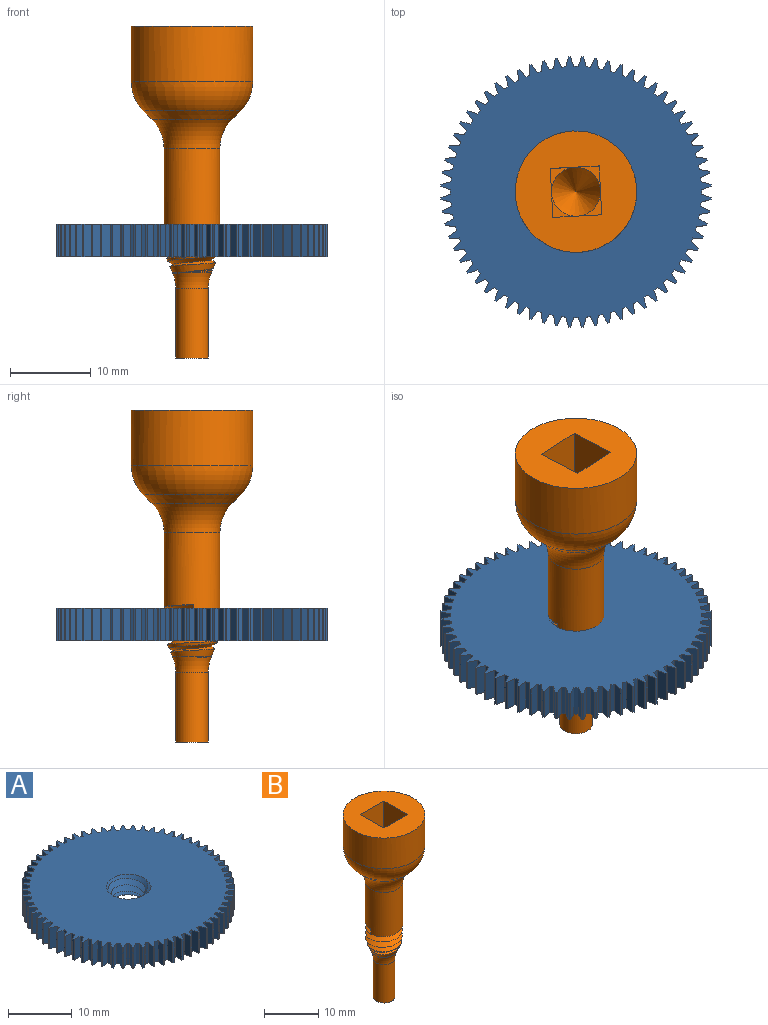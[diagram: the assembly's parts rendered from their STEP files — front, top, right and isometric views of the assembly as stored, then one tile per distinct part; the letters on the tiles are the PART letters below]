
ASSEMBLY  parts=2 mates=1
PART A: 262 faces, bbox 33.4x33.4x5.5 mm
  f0: plane 4x1.22mm, normal (-0.25,0.97,0), area 5.1mm2, adj f1,f255,f256,f257
  f1: cylinder r=15.5mm len=4mm, axis (0,0,-1), area 2.1mm2, adj f0,f2,f255,f257
  f2: plane 4x1.14mm, normal (-0.43,-0.9,0), area 5.1mm2, adj f1,f3,f255,f257
  f3: plane 4x0.24mm, normal (-0.99,0.15,0), area 1mm2, adj f2,f4,f255,f257
  f4: plane 4x1.25mm, normal (-0.15,0.99,0), area 5.1mm2, adj f3,f5,f255,f257
  f5: cylinder r=15.5mm len=4mm, axis (0,0,-1), area 2.1mm2, adj f4,f6,f255,f257
  f6: plane 4x1.08mm, normal (-0.52,-0.85,0), area 5.1mm2, adj f5,f7,f255,f257
  f7: plane 4x0.23mm, normal (-0.97,0.24,0), area 1mm2, adj f6,f8,f255,f257
  f8: plane 4x1.26mm, normal (-0.05,1,0), area 5.1mm2, adj f7,f9,f255,f257
  f9: cylinder r=15.5mm len=4mm, axis (0,0,-1), area 2.1mm2, adj f8,f10,f255,f257
  f10: plane 4x1.01mm, normal (-0.6,-0.8,0), area 5.1mm2, adj f9,f11,f255,f257
  f11: plane 4x0.23mm, normal (-0.94,0.34,0), area 1mm2, adj f10,f12,f255,f257
  f12: plane 4x1.26mm, normal (0.04,1,0), area 5.1mm2, adj f11,f13,f255,f257
  f13: cylinder r=15.5mm len=4mm, axis (0,0,-1), area 2.1mm2, adj f12,f14,f255,f257
  f14: plane 4x0.93mm, normal (-0.68,-0.74,0), area 5.1mm2, adj f13,f15,f255,f257
  f15: plane 4x0.22mm, normal (-0.9,0.43,0), area 1mm2, adj f14,f16,f255,f257
  f16: plane 4x1.25mm, normal (0.14,0.99,0), area 5.1mm2, adj f15,f17,f255,f257
  f17: cylinder r=15.5mm len=4mm, axis (0,0,-1), area 2.1mm2, adj f16,f18,f255,f257
  f18: plane 4x0.94mm, normal (-0.74,-0.67,0), area 5.1mm2, adj f17,f19,f255,f257
  f19: plane 4x0.21mm, normal (-0.86,0.51,0), area 1mm2, adj f18,f20,f255,f257
  f20: plane 4x1.23mm, normal (0.24,0.97,0), area 5.1mm2, adj f19,f21,f255,f257
  f21: cylinder r=15.5mm len=4mm, axis (0,0,-1), area 2.1mm2, adj f20,f22,f255,f257
  f22: plane 4x1.02mm, normal (-0.81,-0.59,0), area 5.1mm2, adj f21,f23,f255,f257
  f23: plane 4x0.19mm, normal (-0.8,0.6,0), area 1mm2, adj f22,f24,f255,f257
  f24: plane 4x1.19mm, normal (0.33,0.94,0), area 5.1mm2, adj f23,f25,f255,f257
  f25: cylinder r=15.5mm len=4mm, axis (0,0,-1), area 2.1mm2, adj f24,f26,f255,f257
  f26: plane 4x1.09mm, normal (-0.86,-0.51,0), area 5.1mm2, adj f25,f27,f255,f257
  f27: plane 4x0.18mm, normal (-0.74,0.67,0), area 1mm2, adj f26,f28,f255,f257
  f28: plane 4x1.15mm, normal (0.42,0.91,0), area 5.1mm2, adj f27,f29,f255,f257
  f29: cylinder r=15.5mm len=4mm, axis (0,0,-1), area 2.1mm2, adj f28,f30,f255,f257
  f30: plane 4x1.15mm, normal (-0.91,-0.42,0), area 5.1mm2, adj f29,f31,f255,f257
  f31: plane 4x0.18mm, normal (-0.67,0.74,0), area 1mm2, adj f30,f32,f255,f257
  f32: plane 4x1.09mm, normal (0.51,0.86,0), area 5.1mm2, adj f31,f33,f255,f257
  f33: cylinder r=15.5mm len=4mm, axis (0,0,-1), area 2.1mm2, adj f32,f34,f255,f257
  f34: plane 4x1.19mm, normal (-0.94,-0.33,0), area 5.1mm2, adj f33,f35,f255,f257
  f35: plane 4x0.19mm, normal (-0.6,0.8,0), area 1mm2, adj f34,f36,f255,f257
  f36: plane 4x1.02mm, normal (0.59,0.81,0), area 5.1mm2, adj f35,f37,f255,f257
  f37: cylinder r=15.5mm len=4mm, axis (0,0,-1), area 2.1mm2, adj f36,f38,f255,f257
  f38: plane 4x1.23mm, normal (-0.97,-0.24,0), area 5.1mm2, adj f37,f39,f255,f257
  f39: plane 4x0.21mm, normal (-0.51,0.86,0), area 1mm2, adj f38,f40,f255,f257
  f40: plane 4x0.94mm, normal (0.67,0.74,0), area 5.1mm2, adj f39,f41,f255,f257
  f41: cylinder r=15.5mm len=4mm, axis (0,0,-1), area 2.1mm2, adj f40,f42,f255,f257
  f42: plane 4x1.25mm, normal (-0.99,-0.14,0), area 5.1mm2, adj f41,f43,f255,f257
  f43: plane 4x0.22mm, normal (-0.43,0.9,0), area 1mm2, adj f42,f44,f255,f257
  f44: plane 4x0.93mm, normal (0.74,0.68,0), area 5.1mm2, adj f43,f45,f255,f257
  f45: cylinder r=15.5mm len=4mm, axis (0,0,-1), area 2.1mm2, adj f44,f46,f255,f257
  f46: plane 4x1.26mm, normal (-1,-0.04,0), area 5.1mm2, adj f45,f47,f255,f257
  f47: plane 4x0.23mm, normal (-0.34,0.94,0), area 1mm2, adj f46,f48,f255,f257
  f48: plane 4x1.01mm, normal (0.8,0.6,0), area 5.1mm2, adj f47,f49,f255,f257
  f49: cylinder r=15.5mm len=4mm, axis (0,0,-1), area 2.1mm2, adj f48,f50,f255,f257
  f50: plane 4x1.26mm, normal (-1,0.05,0), area 5.1mm2, adj f49,f51,f255,f257
  f51: plane 4x0.23mm, normal (-0.24,0.97,0), area 1mm2, adj f50,f52,f255,f257
  f52: plane 4x1.08mm, normal (0.85,0.52,0), area 5.1mm2, adj f51,f53,f255,f257
  f53: cylinder r=15.5mm len=4mm, axis (0,0,-1), area 2.1mm2, adj f52,f54,f255,f257
  f54: plane 4x1.25mm, normal (-0.99,0.15,0), area 5.1mm2, adj f53,f55,f255,f257
  f55: plane 4x0.24mm, normal (-0.15,0.99,0), area 1mm2, adj f54,f56,f255,f257
  f56: plane 4x1.14mm, normal (0.9,0.43,0), area 5.1mm2, adj f55,f57,f255,f257
  f57: cylinder r=15.5mm len=4mm, axis (0,0,-1), area 2.1mm2, adj f56,f58,f255,f257
  f58: plane 4x1.22mm, normal (-0.97,0.25,0), area 5.1mm2, adj f57,f59,f255,f257
  f59: plane 4x0.24mm, normal (-0.05,1,0), area 1mm2, adj f58,f60,f255,f257
  f60: plane 4x1.19mm, normal (0.94,0.34,0), area 5.1mm2, adj f59,f61,f255,f257
  f61: cylinder r=15.5mm len=4mm, axis (0,0,-1), area 2.1mm2, adj f60,f62,f255,f257
  f62: plane 4x1.19mm, normal (-0.94,0.34,0), area 5.1mm2, adj f61,f63,f255,f257
  f63: plane 4x0.24mm, normal (0.05,1,0), area 1mm2, adj f62,f64,f255,f257
  f64: plane 4x1.22mm, normal (0.97,0.25,0), area 5.1mm2, adj f63,f65,f255,f257
  f65: cylinder r=15.5mm len=4mm, axis (0,0,-1), area 2.1mm2, adj f64,f66,f255,f257
  f66: plane 4x1.14mm, normal (-0.9,0.43,0), area 5.1mm2, adj f65,f67,f255,f257
  f67: plane 4x0.24mm, normal (0.15,0.99,0), area 1mm2, adj f66,f68,f255,f257
  f68: plane 4x1.25mm, normal (0.99,0.15,0), area 5.1mm2, adj f67,f69,f255,f257
  f69: cylinder r=15.5mm len=4mm, axis (0,0,-1), area 2.1mm2, adj f68,f70,f255,f257
  f70: plane 4x1.08mm, normal (-0.85,0.52,0), area 5.1mm2, adj f69,f71,f255,f257
  f71: plane 4x0.23mm, normal (0.24,0.97,0), area 1mm2, adj f70,f72,f255,f257
  f72: plane 4x1.26mm, normal (1,0.05,0), area 5.1mm2, adj f71,f73,f255,f257
  f73: cylinder r=15.5mm len=4mm, axis (0,0,-1), area 2.1mm2, adj f72,f74,f255,f257
  f74: plane 4x1.01mm, normal (-0.8,0.6,0), area 5.1mm2, adj f73,f75,f255,f257
  f75: plane 4x0.23mm, normal (0.34,0.94,0), area 1mm2, adj f74,f76,f255,f257
  f76: plane 4x1.26mm, normal (1,-0.04,0), area 5.1mm2, adj f75,f77,f255,f257
  f77: cylinder r=15.5mm len=4mm, axis (0,0,-1), area 2.1mm2, adj f76,f78,f255,f257
  f78: plane 4x0.93mm, normal (-0.74,0.68,0), area 5.1mm2, adj f77,f79,f255,f257
  f79: plane 4x0.22mm, normal (0.43,0.9,0), area 1mm2, adj f78,f80,f255,f257
  f80: plane 4x1.25mm, normal (0.99,-0.14,0), area 5.1mm2, adj f79,f81,f255,f257
  f81: cylinder r=15.5mm len=4mm, axis (0,0,-1), area 2.1mm2, adj f80,f82,f255,f257
  f82: plane 4x0.94mm, normal (-0.67,0.74,0), area 5.1mm2, adj f81,f83,f255,f257
  f83: plane 4x0.21mm, normal (0.51,0.86,0), area 1mm2, adj f82,f84,f255,f257
  f84: plane 4x1.23mm, normal (0.97,-0.24,0), area 5.1mm2, adj f83,f85,f255,f257
  f85: cylinder r=15.5mm len=4mm, axis (0,0,-1), area 2.1mm2, adj f84,f86,f255,f257
  f86: plane 4x1.02mm, normal (-0.59,0.81,0), area 5.1mm2, adj f85,f87,f255,f257
  f87: plane 4x0.19mm, normal (0.6,0.8,0), area 1mm2, adj f86,f88,f255,f257
  f88: plane 4x1.19mm, normal (0.94,-0.33,0), area 5.1mm2, adj f87,f89,f255,f257
  f89: cylinder r=15.5mm len=4mm, axis (0,0,-1), area 2.1mm2, adj f88,f90,f255,f257
  f90: plane 4x1.09mm, normal (-0.51,0.86,0), area 5.1mm2, adj f89,f91,f255,f257
  f91: plane 4x0.18mm, normal (0.67,0.74,0), area 1mm2, adj f90,f92,f255,f257
  f92: plane 4x1.15mm, normal (0.91,-0.42,0), area 5.1mm2, adj f91,f93,f255,f257
  f93: cylinder r=15.5mm len=4mm, axis (0,0,-1), area 2.1mm2, adj f92,f94,f255,f257
  f94: plane 4x1.15mm, normal (-0.42,0.91,0), area 5.1mm2, adj f93,f95,f255,f257
  f95: plane 4x0.18mm, normal (0.74,0.67,0), area 1mm2, adj f94,f96,f255,f257
  f96: plane 4x1.09mm, normal (0.86,-0.51,0), area 5.1mm2, adj f95,f97,f255,f257
  f97: cylinder r=15.5mm len=4mm, axis (0,0,-1), area 2.1mm2, adj f96,f98,f255,f257
  f98: plane 4x1.19mm, normal (-0.33,0.94,0), area 5.1mm2, adj f97,f99,f255,f257
  f99: plane 4x0.19mm, normal (0.8,0.6,0), area 1mm2, adj f98,f100,f255,f257
  f100: plane 4x1.02mm, normal (0.81,-0.59,0), area 5.1mm2, adj f99,f101,f255,f257
  f101: cylinder r=15.5mm len=4mm, axis (0,0,-1), area 2.1mm2, adj f100,f102,f255,f257
  f102: plane 4x1.23mm, normal (-0.24,0.97,0), area 5.1mm2, adj f101,f103,f255,f257
  f103: plane 4x0.21mm, normal (0.86,0.51,0), area 1mm2, adj f102,f104,f255,f257
  f104: plane 4x0.94mm, normal (0.74,-0.67,0), area 5.1mm2, adj f103,f105,f255,f257
  f105: cylinder r=15.5mm len=4mm, axis (0,0,-1), area 2.1mm2, adj f104,f106,f255,f257
  f106: plane 4x1.25mm, normal (-0.14,0.99,0), area 5.1mm2, adj f105,f107,f255,f257
  f107: plane 4x0.22mm, normal (0.9,0.43,0), area 1mm2, adj f106,f108,f255,f257
  f108: plane 4x0.93mm, normal (0.68,-0.74,0), area 5.1mm2, adj f107,f109,f255,f257
  f109: cylinder r=15.5mm len=4mm, axis (0,0,-1), area 2.1mm2, adj f108,f110,f255,f257
  f110: plane 4x1.26mm, normal (-0.04,1,0), area 5.1mm2, adj f109,f111,f255,f257
  f111: plane 4x0.23mm, normal (0.94,0.34,0), area 1mm2, adj f110,f112,f255,f257
  f112: plane 4x1.01mm, normal (0.6,-0.8,0), area 5.1mm2, adj f111,f113,f255,f257
  f113: cylinder r=15.5mm len=4mm, axis (0,0,-1), area 2.1mm2, adj f112,f114,f255,f257
  f114: plane 4x1.26mm, normal (0.05,1,0), area 5.1mm2, adj f113,f115,f255,f257
  f115: plane 4x0.23mm, normal (0.97,0.24,0), area 1mm2, adj f114,f116,f255,f257
  f116: plane 4x1.08mm, normal (0.52,-0.85,0), area 5.1mm2, adj f115,f117,f255,f257
  f117: cylinder r=15.5mm len=4mm, axis (0,0,-1), area 2.1mm2, adj f116,f118,f255,f257
  f118: plane 4x1.25mm, normal (0.15,0.99,0), area 5.1mm2, adj f117,f119,f255,f257
  f119: plane 4x0.24mm, normal (0.99,0.15,0), area 1mm2, adj f118,f120,f255,f257
  f120: plane 4x1.14mm, normal (0.43,-0.9,0), area 5.1mm2, adj f119,f121,f255,f257
  f121: cylinder r=15.5mm len=4mm, axis (0,0,-1), area 2.1mm2, adj f120,f122,f255,f257
  f122: plane 4x1.22mm, normal (0.25,0.97,0), area 5.1mm2, adj f121,f123,f255,f257
  f123: plane 4x0.24mm, normal (1,0.05,0), area 1mm2, adj f122,f124,f255,f257
  f124: plane 4x1.19mm, normal (0.34,-0.94,0), area 5.1mm2, adj f123,f125,f255,f257
  f125: cylinder r=15.5mm len=4mm, axis (0,0,-1), area 2.1mm2, adj f124,f126,f255,f257
  f126: plane 4x1.19mm, normal (0.34,0.94,0), area 5.1mm2, adj f125,f127,f255,f257
  f127: plane 4x0.24mm, normal (1,-0.05,0), area 1mm2, adj f126,f128,f255,f257
  f128: plane 4x1.22mm, normal (0.25,-0.97,0), area 5.1mm2, adj f127,f129,f255,f257
  f129: cylinder r=15.5mm len=4mm, axis (0,0,-1), area 2.1mm2, adj f128,f130,f255,f257
  f130: plane 4x1.14mm, normal (0.43,0.9,0), area 5.1mm2, adj f129,f131,f255,f257
  f131: plane 4x0.24mm, normal (0.99,-0.15,0), area 1mm2, adj f130,f132,f255,f257
  f132: plane 4x1.25mm, normal (0.15,-0.99,0), area 5.1mm2, adj f131,f133,f255,f257
  f133: cylinder r=15.5mm len=4mm, axis (0,0,-1), area 2.1mm2, adj f132,f134,f255,f257
  f134: plane 4x1.08mm, normal (0.52,0.85,0), area 5.1mm2, adj f133,f135,f255,f257
  f135: plane 4x0.23mm, normal (0.97,-0.24,0), area 1mm2, adj f134,f136,f255,f257
  f136: plane 4x1.26mm, normal (0.05,-1,0), area 5.1mm2, adj f135,f137,f255,f257
  f137: cylinder r=15.5mm len=4mm, axis (0,0,-1), area 2.1mm2, adj f136,f138,f255,f257
  f138: plane 4x1.01mm, normal (0.6,0.8,0), area 5.1mm2, adj f137,f139,f255,f257
  f139: plane 4x0.23mm, normal (0.94,-0.34,0), area 1mm2, adj f138,f140,f255,f257
  f140: plane 4x1.26mm, normal (-0.04,-1,0), area 5.1mm2, adj f139,f141,f255,f257
  f141: cylinder r=15.5mm len=4mm, axis (0,0,-1), area 2.1mm2, adj f140,f142,f255,f257
  f142: plane 4x0.93mm, normal (0.68,0.74,0), area 5.1mm2, adj f141,f143,f255,f257
  f143: plane 4x0.22mm, normal (0.9,-0.43,0), area 1mm2, adj f142,f144,f255,f257
  f144: plane 4x1.25mm, normal (-0.14,-0.99,0), area 5.1mm2, adj f143,f145,f255,f257
  f145: cylinder r=15.5mm len=4mm, axis (0,0,-1), area 2.1mm2, adj f144,f146,f255,f257
  f146: plane 4x0.94mm, normal (0.74,0.67,0), area 5.1mm2, adj f145,f147,f255,f257
  f147: plane 4x0.21mm, normal (0.86,-0.51,0), area 1mm2, adj f146,f148,f255,f257
  f148: plane 4x1.23mm, normal (-0.24,-0.97,0), area 5.1mm2, adj f147,f149,f255,f257
  f149: cylinder r=15.5mm len=4mm, axis (0,0,-1), area 2.1mm2, adj f148,f150,f255,f257
  f150: plane 4x1.02mm, normal (0.81,0.59,0), area 5.1mm2, adj f149,f151,f255,f257
  f151: plane 4x0.19mm, normal (0.8,-0.6,0), area 1mm2, adj f150,f152,f255,f257
  f152: plane 4x1.19mm, normal (-0.33,-0.94,0), area 5.1mm2, adj f151,f153,f255,f257
  f153: cylinder r=15.5mm len=4mm, axis (0,0,-1), area 2.1mm2, adj f152,f154,f255,f257
  f154: plane 4x1.09mm, normal (0.86,0.51,0), area 5.1mm2, adj f153,f155,f255,f257
  f155: plane 4x0.18mm, normal (0.74,-0.67,0), area 1mm2, adj f154,f156,f255,f257
  f156: plane 4x1.15mm, normal (-0.42,-0.91,0), area 5.1mm2, adj f155,f157,f255,f257
  f157: cylinder r=15.5mm len=4mm, axis (0,0,-1), area 2.1mm2, adj f156,f158,f255,f257
  f158: plane 4x1.15mm, normal (0.91,0.42,0), area 5.1mm2, adj f157,f159,f255,f257
  f159: plane 4x0.18mm, normal (0.67,-0.74,0), area 1mm2, adj f158,f160,f255,f257
  f160: plane 4x1.09mm, normal (-0.51,-0.86,0), area 5.1mm2, adj f159,f161,f255,f257
  f161: cylinder r=15.5mm len=4mm, axis (0,0,-1), area 2.1mm2, adj f160,f162,f255,f257
  f162: plane 4x1.19mm, normal (0.94,0.33,0), area 5.1mm2, adj f161,f163,f255,f257
  f163: plane 4x0.19mm, normal (0.6,-0.8,0), area 1mm2, adj f162,f164,f255,f257
  f164: plane 4x1.02mm, normal (-0.59,-0.81,0), area 5.1mm2, adj f163,f165,f255,f257
  f165: cylinder r=15.5mm len=4mm, axis (0,0,-1), area 2.1mm2, adj f164,f166,f255,f257
  f166: plane 4x1.23mm, normal (0.97,0.24,0), area 5.1mm2, adj f165,f167,f255,f257
  f167: plane 4x0.21mm, normal (0.51,-0.86,0), area 1mm2, adj f166,f168,f255,f257
  f168: plane 4x0.94mm, normal (-0.67,-0.74,0), area 5.1mm2, adj f167,f169,f255,f257
  f169: cylinder r=15.5mm len=4mm, axis (0,0,-1), area 2.1mm2, adj f168,f170,f255,f257
  f170: plane 4x1.25mm, normal (0.99,0.14,0), area 5.1mm2, adj f169,f171,f255,f257
  f171: plane 4x0.22mm, normal (0.43,-0.9,0), area 1mm2, adj f170,f172,f255,f257
  f172: plane 4x0.93mm, normal (-0.74,-0.68,0), area 5.1mm2, adj f171,f173,f255,f257
  f173: cylinder r=15.5mm len=4mm, axis (0,0,-1), area 2.1mm2, adj f172,f174,f255,f257
  f174: plane 4x1.26mm, normal (1,0.04,0), area 5.1mm2, adj f173,f175,f255,f257
  f175: plane 4x0.23mm, normal (0.34,-0.94,0), area 1mm2, adj f174,f176,f255,f257
  f176: plane 4x1.01mm, normal (-0.8,-0.6,0), area 5.1mm2, adj f175,f177,f255,f257
  f177: cylinder r=15.5mm len=4mm, axis (0,0,-1), area 2.1mm2, adj f176,f178,f255,f257
  f178: plane 4x1.26mm, normal (1,-0.05,0), area 5.1mm2, adj f177,f179,f255,f257
  f179: plane 4x0.23mm, normal (0.24,-0.97,0), area 1mm2, adj f178,f180,f255,f257
  f180: plane 4x1.08mm, normal (-0.85,-0.52,0), area 5.1mm2, adj f179,f181,f255,f257
  f181: cylinder r=15.5mm len=4mm, axis (0,0,-1), area 2.1mm2, adj f180,f182,f255,f257
  f182: plane 4x1.25mm, normal (0.99,-0.15,0), area 5.1mm2, adj f181,f183,f255,f257
  f183: plane 4x0.24mm, normal (0.15,-0.99,0), area 1mm2, adj f182,f184,f255,f257
  f184: plane 4x1.14mm, normal (-0.9,-0.43,0), area 5.1mm2, adj f183,f185,f255,f257
  f185: cylinder r=15.5mm len=4mm, axis (0,0,-1), area 2.1mm2, adj f184,f186,f255,f257
  f186: plane 4x1.22mm, normal (0.97,-0.25,0), area 5.1mm2, adj f185,f187,f255,f257
  f187: plane 4x0.24mm, normal (0.05,-1,0), area 1mm2, adj f186,f188,f255,f257
  f188: plane 4x1.19mm, normal (-0.94,-0.34,0), area 5.1mm2, adj f187,f189,f255,f257
  f189: cylinder r=15.5mm len=4mm, axis (0,0,-1), area 2.1mm2, adj f188,f190,f255,f257
  f190: plane 4x1.19mm, normal (0.94,-0.34,0), area 5.1mm2, adj f189,f191,f255,f257
  f191: plane 4x0.24mm, normal (-0.05,-1,0), area 1mm2, adj f190,f192,f255,f257
  f192: plane 4x1.22mm, normal (-0.97,-0.25,0), area 5.1mm2, adj f191,f193,f255,f257
  f193: cylinder r=15.5mm len=4mm, axis (0,0,-1), area 2.1mm2, adj f192,f194,f255,f257
  f194: plane 4x1.14mm, normal (0.9,-0.43,0), area 5.1mm2, adj f193,f195,f255,f257
  f195: plane 4x0.24mm, normal (-0.15,-0.99,0), area 1mm2, adj f194,f196,f255,f257
  f196: plane 4x1.25mm, normal (-0.99,-0.15,0), area 5.1mm2, adj f195,f197,f255,f257
  f197: cylinder r=15.5mm len=4mm, axis (0,0,-1), area 2.1mm2, adj f196,f198,f255,f257
  f198: plane 4x1.08mm, normal (0.85,-0.52,0), area 5.1mm2, adj f197,f199,f255,f257
  f199: plane 4x0.23mm, normal (-0.24,-0.97,0), area 1mm2, adj f198,f200,f255,f257
  f200: plane 4x1.26mm, normal (-1,-0.05,0), area 5.1mm2, adj f199,f201,f255,f257
  f201: cylinder r=15.5mm len=4mm, axis (0,0,-1), area 2.1mm2, adj f200,f202,f255,f257
  f202: plane 4x1.01mm, normal (0.8,-0.6,0), area 5.1mm2, adj f201,f203,f255,f257
  f203: plane 4x0.23mm, normal (-0.34,-0.94,0), area 1mm2, adj f202,f204,f255,f257
  f204: plane 4x1.26mm, normal (-1,0.04,0), area 5.1mm2, adj f203,f205,f255,f257
  f205: cylinder r=15.5mm len=4mm, axis (0,0,-1), area 2.1mm2, adj f204,f206,f255,f257
  f206: plane 4x0.93mm, normal (0.74,-0.68,0), area 5.1mm2, adj f205,f207,f255,f257
  f207: plane 4x0.22mm, normal (-0.43,-0.9,0), area 1mm2, adj f206,f208,f255,f257
  f208: plane 4x1.25mm, normal (-0.99,0.14,0), area 5.1mm2, adj f207,f209,f255,f257
  f209: cylinder r=15.5mm len=4mm, axis (0,0,-1), area 2.1mm2, adj f208,f210,f255,f257
  f210: plane 4x0.94mm, normal (0.67,-0.74,0), area 5.1mm2, adj f209,f211,f255,f257
  f211: plane 4x0.21mm, normal (-0.51,-0.86,0), area 1mm2, adj f210,f212,f255,f257
  f212: plane 4x1.23mm, normal (-0.97,0.24,0), area 5.1mm2, adj f211,f213,f255,f257
  f213: cylinder r=15.5mm len=4mm, axis (0,0,-1), area 2.1mm2, adj f212,f214,f255,f257
  f214: plane 4x1.02mm, normal (0.59,-0.81,0), area 5.1mm2, adj f213,f215,f255,f257
  f215: plane 4x0.19mm, normal (-0.6,-0.8,0), area 1mm2, adj f214,f216,f255,f257
  f216: plane 4x1.19mm, normal (-0.94,0.33,0), area 5.1mm2, adj f215,f217,f255,f257
  f217: cylinder r=15.5mm len=4mm, axis (0,0,-1), area 2.1mm2, adj f216,f218,f255,f257
  f218: plane 4x1.09mm, normal (0.51,-0.86,0), area 5.1mm2, adj f217,f219,f255,f257
  f219: plane 4x0.18mm, normal (-0.67,-0.74,0), area 1mm2, adj f218,f220,f255,f257
  f220: plane 4x1.15mm, normal (-0.91,0.42,0), area 5.1mm2, adj f219,f221,f255,f257
  f221: cylinder r=15.5mm len=4mm, axis (0,0,-1), area 2.1mm2, adj f220,f222,f255,f257
  f222: plane 4x1.15mm, normal (0.42,-0.91,0), area 5.1mm2, adj f221,f223,f255,f257
  f223: plane 4x0.18mm, normal (-0.74,-0.67,0), area 1mm2, adj f222,f224,f255,f257
  f224: plane 4x1.09mm, normal (-0.86,0.51,0), area 5.1mm2, adj f223,f225,f255,f257
  f225: cylinder r=15.5mm len=4mm, axis (0,0,-1), area 2.1mm2, adj f224,f226,f255,f257
  f226: plane 4x1.19mm, normal (0.33,-0.94,0), area 5.1mm2, adj f225,f227,f255,f257
  f227: plane 4x0.19mm, normal (-0.8,-0.6,0), area 1mm2, adj f226,f228,f255,f257
  f228: plane 4x1.02mm, normal (-0.81,0.59,0), area 5.1mm2, adj f227,f229,f255,f257
  f229: cylinder r=15.5mm len=4mm, axis (0,0,-1), area 2.1mm2, adj f228,f230,f255,f257
  f230: plane 4x1.23mm, normal (0.24,-0.97,0), area 5.1mm2, adj f229,f231,f255,f257
  f231: plane 4x0.21mm, normal (-0.86,-0.51,0), area 1mm2, adj f230,f232,f255,f257
  f232: plane 4x0.94mm, normal (-0.74,0.67,0), area 5.1mm2, adj f231,f233,f255,f257
  f233: cylinder r=15.5mm len=4mm, axis (0,0,-1), area 2.1mm2, adj f232,f234,f255,f257
  f234: plane 4x1.25mm, normal (0.14,-0.99,0), area 5.1mm2, adj f233,f235,f255,f257
  f235: plane 4x0.22mm, normal (-0.9,-0.43,0), area 1mm2, adj f234,f236,f255,f257
  f236: plane 4x0.93mm, normal (-0.68,0.74,0), area 5.1mm2, adj f235,f237,f255,f257
  f237: cylinder r=15.5mm len=4mm, axis (0,0,-1), area 2.1mm2, adj f236,f238,f255,f257
  f238: plane 4x1.26mm, normal (0.04,-1,0), area 5.1mm2, adj f237,f239,f255,f257
  f239: plane 4x0.23mm, normal (-0.94,-0.34,0), area 1mm2, adj f238,f240,f255,f257
  f240: plane 4x1.01mm, normal (-0.6,0.8,0), area 5.1mm2, adj f239,f241,f255,f257
  f241: cylinder r=15.5mm len=4mm, axis (0,0,-1), area 2.1mm2, adj f240,f242,f255,f257
  f242: plane 4x1.26mm, normal (-0.05,-1,0), area 5.1mm2, adj f241,f243,f255,f257
  f243: plane 4x0.23mm, normal (-0.97,-0.24,0), area 1mm2, adj f242,f244,f255,f257
  f244: plane 4x1.08mm, normal (-0.52,0.85,0), area 5.1mm2, adj f243,f245,f255,f257
  f245: cylinder r=15.5mm len=4mm, axis (0,0,-1), area 2.1mm2, adj f244,f246,f255,f257
  f246: plane 4x1.25mm, normal (-0.15,-0.99,0), area 5.1mm2, adj f245,f247,f255,f257
  f247: plane 4x0.24mm, normal (-0.99,-0.15,0), area 1mm2, adj f246,f248,f255,f257
  f248: plane 4x1.14mm, normal (-0.43,0.9,0), area 5.1mm2, adj f247,f249,f255,f257
  f249: cylinder r=15.5mm len=4mm, axis (0,0,-1), area 2.1mm2, adj f248,f250,f255,f257
  f250: plane 4x1.22mm, normal (-0.25,-0.97,0), area 5.1mm2, adj f249,f251,f255,f257
  f251: plane 4x0.24mm, normal (-1,-0.05,0), area 1mm2, adj f250,f252,f255,f257
  f252: plane 4x1.19mm, normal (-0.34,0.94,0), area 5.1mm2, adj f251,f253,f255,f257
  f253: cylinder r=15.5mm len=4mm, axis (0,0,-1), area 2.1mm2, adj f252,f254,f255,f257
  f254: plane 4x1.19mm, normal (-0.34,-0.94,0), area 5.1mm2, adj f253,f255,f256,f257
  f255: plane 33.42x33.42mm, normal (0,0,-1), area 764.9mm2, adj f0,f1,f2,f3,f4,f5,f6,f7
  f256: plane 4x0.24mm, normal (-1,0.05,0), area 1mm2, adj f0,f254,f255,f257
  f257: plane 33.42x33.42mm, normal (0,0,1), area 764.9mm2, adj f0,f1,f2,f3,f4,f5,f6,f7
  f258: cone r=3.4mm half-angle=45deg, axis (0,0,-1), area 8.8mm2, adj f255,f260,f261
  f259: cone r=2.5mm half-angle=45deg, axis (0,0,1), area 8.8mm2, adj f257,f260,f261
  f260: bspline ~8.37x7.25mm, area 66.9mm2, adj f255,f257,f258,f259,f261
  f261: bspline ~8.37x7.25mm, area 66.8mm2, adj f255,f257,f258,f259,f260
PART B: 23 faces, bbox 18.3x18.3x41 mm
  f0: plane 3.03x3.03mm, normal (0,0,1), area 2mm2, adj f5,f8,f22
  f1: plane 3.03x3.03mm, normal (0,0,1), area 2mm2, adj f5,f6,f22
  f2: plane 3.03x3.03mm, normal (0,0,1), area 2mm2, adj f6,f7,f22
  f3: cylinder r=3.45mm len=10.11mm, axis (0,0,1), area 206.2mm2, adj f13,f14,f16
  f4: cylinder r=7.5mm len=15mm, axis (0,0,-1), area 325.7mm2, adj f9,f12
  f5: plane 7x6.05mm, normal (0,-1,0), area 42.4mm2, adj f0,f1,f6,f8,f9
  f6: plane 7x6.05mm, normal (-1,0,0), area 42.4mm2, adj f1,f2,f5,f7,f9
  f7: plane 7x6.05mm, normal (0,1,0), area 42.4mm2, adj f2,f6,f8,f9,f10
  f8: plane 7x6.05mm, normal (1,0,0), area 42.4mm2, adj f0,f5,f7,f9,f10
  f9: plane 15x15mm, normal (0,0,1), area 140.1mm2, adj f4,f5,f6,f7,f8
  f10: plane 3.03x3.03mm, normal (0,0,1), area 2mm2, adj f7,f8,f22
  f11: cone r=7.5mm half-angle=45.4deg, axis (0,0,1), area 52.1mm2, adj f12,f13
  f12: torus R=2.5mm, axis (0,0,-1), area 173.9mm2, adj f4,f11
  f13: torus R=8.45mm, axis (0,0,1), area 98.4mm2, adj f3,f11
  f14: plane 1.25x1.13mm, normal (0,1,0), area 0.7mm2, adj f3,f15,f16,f17
  f15: bspline ~7.77x6.8mm, area 89.4mm2, adj f14,f16,f17,f20,f21
  f16: bspline ~7.97x6.9mm, area 2.1mm2, adj f3,f14,f15
  f17: bspline ~7.77x6.73mm, area 78.1mm2, adj f14,f15,f20,f21
  f18: plane 4x4mm, normal (0,0,-1), area 12.6mm2, adj f19
  f19: cylinder r=2mm len=8.62mm, axis (0,0,1), area 108.3mm2, adj f18,f20
  f20: torus R=7mm, axis (0,0,1), area 27.4mm2, adj f15,f17,f19,f21
  f21: cone r=3.45mm half-angle=23.5deg, axis (0,0,1), area 18.8mm2, adj f15,f17,f20
  f22: cone r=3.02mm half-angle=28.2deg, axis (0,0,1), area 60.8mm2, adj f0,f1,f2,f10
PLACE A rot(axis=(0,0,1),90deg) t=(-6.42,2.58,-31.54)mm
PLACE B rot(axis=(0,0,1),3deg) t=(-6.43,2.58,-31.05)mm
MATE cylindrical A.f21 <-> B.f19  axis (0,0,1) through (-6.43,2.58,-27.54)mm
